# Revit family: PRD_AR_Snks_MaximaCommercialSink_MAXS200-120
name_source: partatom
category: Plumbing Fixtures
revit_build: Autodesk Revit 2018 (Build: 20190510_1515(x64)
units: mm (PartAtom-declared; Revit-internal decimal feet)

## family parameters
Always vertical = Yes
Cut with Voids When Loaded = No
OmniClass Number = 23.45.05.14.14
OmniClass Title = Sinks/Lavatories
Part Type = Normal
Room Calculation Point = No
Round Connector Dimension = Use Diameter
Shared = No
Work Plane-Based = No

## types (1)
- MAXS200-120
    Accessories = Shelf
    Arrangement = Double bowl sink
    AssetType = Fixed
    BIMObjectName = PRD_AR_KitchenSinks_MaximaCommercialSink_MAXS200-120
    BracketsMaterial = PRD_AR_StainlessSteel_SatinFinished
    Category = Pr_40_20_96_45, Kitchen sinks
    Color = stainless steel
    Constituents = Underframe MAXF120-60
    ConstructionFrameAssembly = Underframe to screw with Franke commercial sink
    ConstructionFrameFinish = satin finished
    ConstructionFrameMaterial = Square tubular leg frame, stainless steel 1.4301
    Description = Commercial sink and underframe welded together, stainless steel, surface satin finished, material thickness 1 mm, two deep drawn seamless welded bowls, without overflow and 80 mm tap ledge, 1 1/2" waste with two part overflow tube consisting of perforated stainless steel tube and plastic tube, 100 mm rear upstand, underframe with 300 mm cover, feet 40 x 40 mm and height adjustable to 25 mm, cross stud on backside for better stability, drilling holes for wall mounting prelasered.
    DrainSize = DN 40 (1 1/2 inch.)
    DurationUnit = year
    Features = stainless steel, 1.00 mm, satin finished
    Finish = satin finished
    GrossWeight = 23.00 kg
    IfcExportAs = IfcSanitaryTerminalType
    IfcExportType = SINK
    Manufacturer = KWC Group AG
    ManufacturerName = KWC Group AG
    ManufacturerURL = www.kwc.com
    Material = stainless steel
    MaterialCode = stainless steel 1.4301
    Model = MAXS200-120
    ModelNumber = 2000057702
    ModelReference = MAXS200-120
    NBSDescription = Commercial stainless steel sinks
    NBSReference = 45-35-15/432
    Name = Maxima catering sink MAXS200-120
    NetWeight = 19.50 kg
    NominalDepth = 600 mm
    NominalHeight = 432 mm  [stored 1.41732 ft]
    NominalWidth = 1200 mm
    OverallDimensionsDepthMaximum = 600 mm
    OverallDimensionsHeightMaximum = 1000 mm  [stored 3.28084 ft]
    OverallDimensionsLengthMaximum = 1200 mm
    ProductInformation = https://pim.kwc.com
    Shape = Rectangular
    SinkMaterial = PRD_AR_StainlessSteel_SatinFinished
    SinkMounting = Other
    SinkType = Rinsing
    Size = 1200 x 432 x 600 mm
    URL = www.kwc.com
    UnderframeMaterial = PRD_AR_StainlessSteel_SatinFinished
    Uniclass2015Code = Pr_40_20_96_45
    Uniclass2015Title = Kitchen sinks
    Uniclass2015Version = Products v1.10
    Version = 1
    WarrantyDurationUnit = year
    WashBowlsDepthMaximum = 300 mm  [stored 0.984252 ft]
    WashBowlsLengthMaximum = 500 mm  [stored 1.64042 ft]
    WashBowlsTapArrangement = 80 mm tap ledge
    WashBowlsWasteArrangement = Right-Back-Corner / Left-Back-Corner
    WashBowlsWasteDiameter = DN 40 (1 1/2 inch.)
    WashBowlsWasteMaterial = stainless steel
    WashBowlsWidthMaximum = 400 mm  [stored 1.31234 ft]
    WasteSize = 40  [stored 0.131234 ft]

note: [stored X ft] marks values corroborated as IEEE doubles in the binary element streams (Revit-internal decimal feet)

## geometry (parser evidence)
native form markers: Sweep x11
no freeform markers — native parametric forms only
